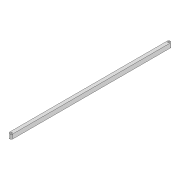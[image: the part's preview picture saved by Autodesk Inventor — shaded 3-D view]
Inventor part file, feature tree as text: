
AUTODESK INVENTOR PART (.ipt)
format: ipt  version: 2022 (Build 260153000, 153)  size: 81,920 bytes
history: native  units: mm
features: extrude x1, sketch x1
ambient origin geometry x8: Origin, YZ Plane, XZ Plane, XY Plane, X Axis, Y Axis, Z Axis, Center Point
bodies: Solid1 (feature_tree)
feature tree (2):
  extrude  "Extrusion1"  Depth=289.365mm
  sketch  "Sketch1"  dims[d0=6.0mm d1=289.365mm d2=3.0mm d3=3.0mm d4=8.0mm d5=0.0mm]
